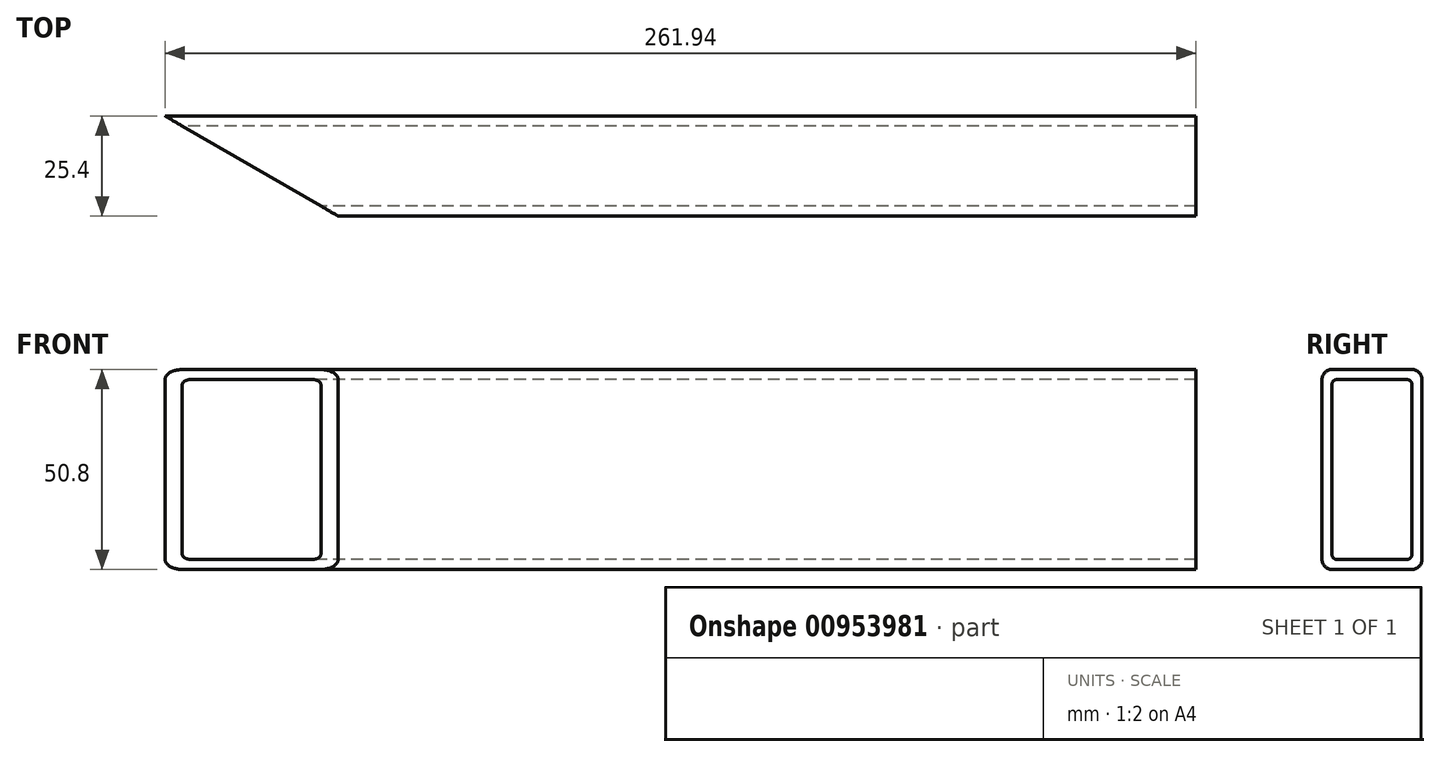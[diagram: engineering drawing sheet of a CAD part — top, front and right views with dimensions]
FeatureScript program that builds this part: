
annotation { "Feature Type Name" : "Feature", "Feature Type Description" : "" }
export const myFeature = defineFeature(function(context is Context, id is Id, definition is map)
    precondition{}
    {
        {
            var Q0;
            Q0=qCreatedBy(makeId("Front.planeOp"),FACE);
            var sketch = newSketch(context, id + "F0", { "sketchPlane" : qUnion([Q0])});
            skLineSegment(sketch, "E0.bottom", {"start": v(130.97, -25.4) * mm, "end": v(-130.97, -25.4) * mm});
            skLineSegment(sketch, "E0.top", {"start": v(130.97, 25.4) * mm, "end": v(-130.97, 25.4) * mm});
            skLineSegment(sketch, "E0.left", {"start": v(130.97, -25.4) * mm, "end": v(130.97, 25.4) * mm});
            skLineSegment(sketch, "E0.right", {"start": v(-130.97, -25.4) * mm, "end": v(-130.97, 25.4) * mm});
            skPoint(sketch, "E0.middle", {"position": v(0, 0) * mm});
            skSolve(sketch);
        }
        {
            var Q0;
            Q0=makeQuery(id+"F0.imprint","IMPRINT",FACE,{"disambiguationData":[TD([[makeQuery(id+"F0.imprint","IMPRINT",EDGE,{"derivedFrom":sQuery(id+"F0.wireOp",EDGE,"E0.bottom")}),-1.0]])]});
            extrude(context, id + "F1", {"entities" : qUnion([Q0]), "endBound" : BoundingType.SYMMETRIC, "depth" : 25.4 * mm, "offsetDistance" : 25.4 * mm});
        }
        {
            var Q0;
            Q0=makeQuery(id+"F1.opExtrude","SWEPT_FACE",FACE,{"disambiguationData":[OSD([sQuery(id+"F0.wireOp",EDGE,"E0.right")])]});
            var Q1;
            Q1=makeQuery(id+"F1.opExtrude","SWEPT_FACE",FACE,{"disambiguationData":[OSD([sQuery(id+"F0.wireOp",EDGE,"E0.left")])]});
            shell(context, id + "F2", {"entities" : qUnion([Q0, Q1]), "thickness" : 2.54 * mm});
        }
        {
            var Q0;
            Q0=makeQuery(id+"F1.opExtrude","SWEPT_FACE",FACE,{"disambiguationData":[OSD([sQuery(id+"F0.wireOp",EDGE,"E0.top")])]});
            var sketch = newSketch(context, id + "F3", { "sketchPlane" : qUnion([Q0])});
            skLineSegment(sketch, "E1", {"start": v(-130.97, 12.7) * mm, "end": v(-86.97, -12.7) * mm});
            skLineSegment(sketch, "E2", {"start": v(-86.97, -12.7) * mm, "end": v(-130.97, -12.7) * mm});
            skLineSegment(sketch, "E3", {"start": v(-130.97, -12.7) * mm, "end": v(-130.97, 12.7) * mm});
            skSolve(sketch);
        }
        {
            var Q0;
            Q0=makeQuery(id+"F3.imprint","IMPRINT",FACE,{"disambiguationData":[TD([[makeQuery(id+"F3.imprint","IMPRINT",EDGE,{"derivedFrom":sQuery(id+"F3.wireOp",EDGE,"E1")}),-1.0]])]});
            extrude(context, id + "F4", {"entities" : qUnion([Q0]), "operationType" : NewBodyOperationType.REMOVE, "endBound" : BoundingType.THROUGH_ALL, "oppositeDirection" : true, "depth" : 25.4 * mm, "offsetDistance" : 25.4 * mm});
        }
        {
            var Q0;
            {var subQ0=sQuery(id+"F0.wireOp",EDGE,"E0.bottom");Q0=makeQuery(id+"F2.opShell","OFFSET_EDGE",EDGE,{"disambiguationData":[OSD([subQ0]),TDD([makeQuery(id+"F1.opExtrude","CAP_EDGE",EDGE,{"disambiguationData":[OSD([subQ0])],"isStart":true})])]});}
            var Q1;
            {var subQ0=sQuery(id+"F0.wireOp",EDGE,"E0.top");Q1=makeQuery(id+"F2.opShell","OFFSET_EDGE",EDGE,{"disambiguationData":[OSD([subQ0]),TDD([makeQuery(id+"F1.opExtrude","CAP_EDGE",EDGE,{"disambiguationData":[OSD([subQ0])],"isStart":true})])]});}
            var Q2;
            {var subQ0=sQuery(id+"F0.wireOp",EDGE,"E0.top");Q2=makeQuery(id+"F2.opShell","OFFSET_EDGE",EDGE,{"disambiguationData":[OSD([subQ0]),TDD([makeQuery(id+"F1.opExtrude","CAP_EDGE",EDGE,{"disambiguationData":[OSD([subQ0])],"isStart":false})])]});}
            var Q3;
            {var subQ0=sQuery(id+"F0.wireOp",EDGE,"E0.bottom");Q3=makeQuery(id+"F2.opShell","OFFSET_EDGE",EDGE,{"disambiguationData":[OSD([subQ0]),TDD([makeQuery(id+"F1.opExtrude","CAP_EDGE",EDGE,{"disambiguationData":[OSD([subQ0])],"isStart":false})])]});}
            fillet(context, id + "F5", {"entities" : qUnion([Q0, Q1, Q2, Q3]), "radius" : 1.27 * mm, "tangentPropagation" : true, "allowEdgeOverflow" : false});
        }
        {
            var Q0;
            Q0=makeQuery(id+"F1.opExtrude","CAP_EDGE",EDGE,{"disambiguationData":[OSD([sQuery(id+"F0.wireOp",EDGE,"E0.top")])],"isStart":false});
            var Q1;
            Q1=makeQuery(id+"F1.opExtrude","CAP_EDGE",EDGE,{"disambiguationData":[OSD([sQuery(id+"F0.wireOp",EDGE,"E0.top")])],"isStart":true});
            var Q2;
            Q2=makeQuery(id+"F1.opExtrude","CAP_EDGE",EDGE,{"disambiguationData":[OSD([sQuery(id+"F0.wireOp",EDGE,"E0.bottom")])],"isStart":true});
            var Q3;
            Q3=makeQuery(id+"F1.opExtrude","CAP_EDGE",EDGE,{"disambiguationData":[OSD([sQuery(id+"F0.wireOp",EDGE,"E0.bottom")])],"isStart":false});
            fillet(context, id + "F6", {"entities" : qUnion([Q0, Q1, Q2, Q3]), "radius" : 2.54 * mm, "tangentPropagation" : true, "allowEdgeOverflow" : false});
        }
    });
